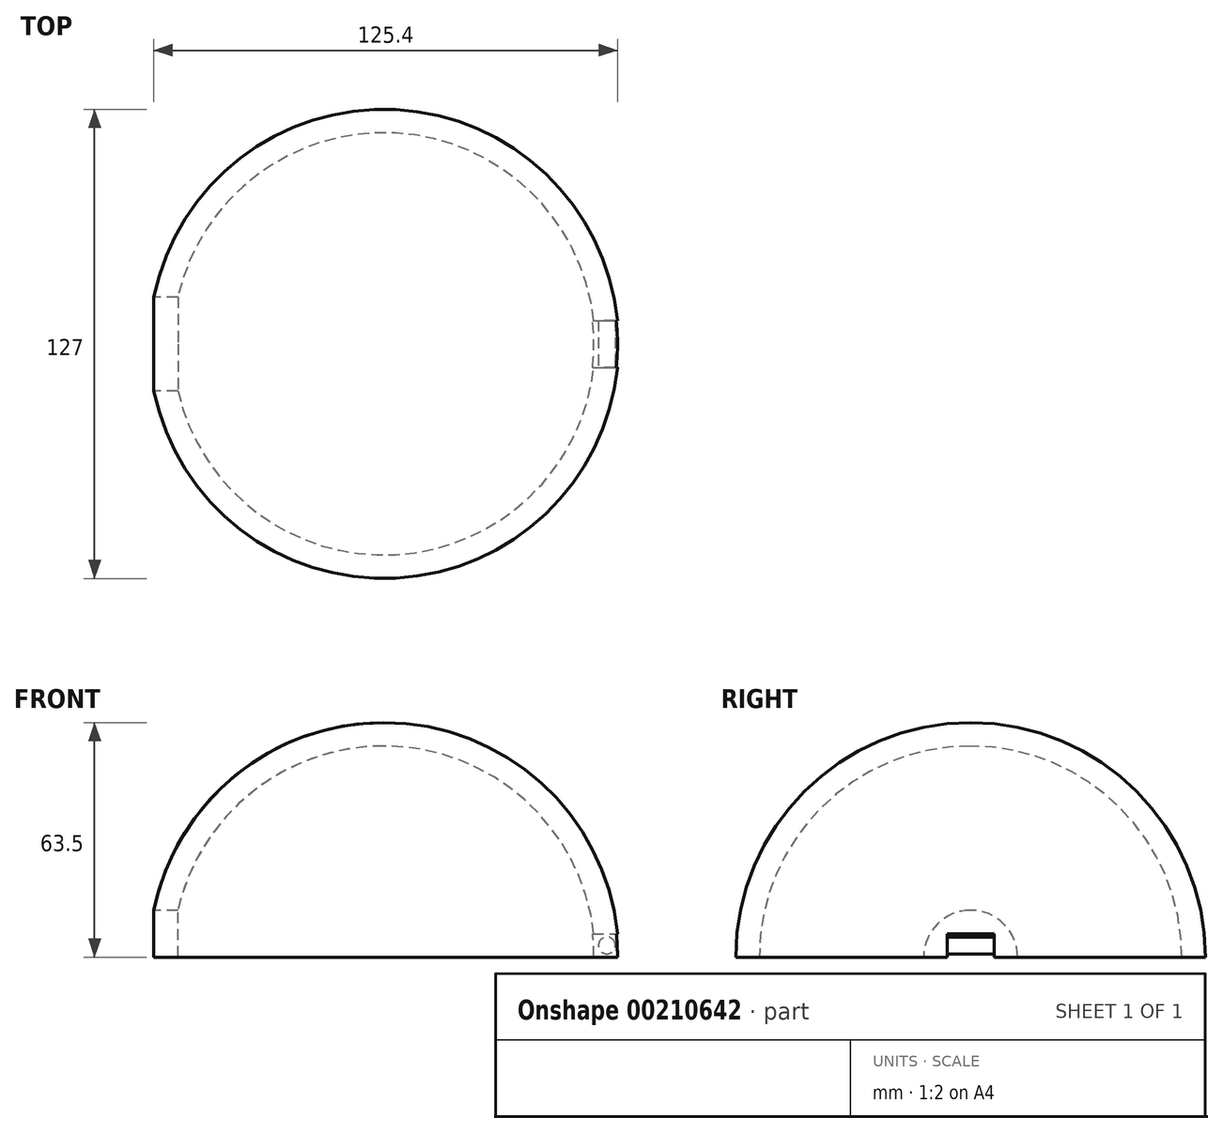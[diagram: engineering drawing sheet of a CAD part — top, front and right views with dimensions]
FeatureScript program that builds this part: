
annotation { "Feature Type Name" : "Feature", "Feature Type Description" : "" }
export const myFeature = defineFeature(function(context is Context, id is Id, definition is map)
    precondition{}
    {
        {
            var Q0;
            Q0=qCreatedBy(makeId("Front.planeOp"),FACE);
            var sketch = newSketch(context, id + "F0", { "sketchPlane" : qUnion([Q0])});
            skArc(sketch, "E0", {"start": v(0, 63.5) * mm, "mid": v(-44.9, 44.9) * mm, "end": v(-63.5, 0) * mm});
            skLineSegment(sketch, "E1", {"start": v(-63.5, 0) * mm, "end": v(-57.15, 0) * mm});
            skLineSegment(sketch, "E2", {"start": v(0, 57.15) * mm, "end": v(0, 63.5) * mm});
            skArc(sketch, "E3.0", {"start": v(0, 57.15) * mm, "mid": v(-40.41, 40.41) * mm, "end": v(-57.15, 0) * mm});
            skSolve(sketch);
        }
        {
            var Q0;
            Q0=makeQuery(id+"F0.imprint","IMPRINT",FACE,{"disambiguationData":[TD([[makeQuery(id+"F0.imprint","IMPRINT",EDGE,{"derivedFrom":sQuery(id+"F0.wireOp",EDGE,"E0")}),1.0]])]});
            var Q1;
            Q1=sQuery(id+"F0.wireOp",EDGE,"E2");
            revolve(context, id + "F1", {"entities" : qUnion([Q0]), "axis" : qUnion([Q1]), "revolveType" : RevolveType.FULL});
        }
        {
            var Q0;
            Q0=qCreatedBy(makeId("Front.planeOp"),FACE);
            var sketch = newSketch(context, id + "F2", { "sketchPlane" : qUnion([Q0])});
            skArc(sketch, "E4", {"start": v(63.5, 0) * mm, "mid": v(0, 63.5) * mm, "end": v(-63.5, 0) * mm, "construction": true});
            skArc(sketch, "E5", {"start": v(57.15, 0) * mm, "mid": v(0, 57.15) * mm, "end": v(-57.15, 0) * mm, "construction": true});
            skCircle(sketch, "E6", {"center": v(60.33, 3.17) * mm, "radius": 2.29 * mm});
            skLineSegment(sketch, "E7.bottom", {"start": v(55.18, -2) * mm, "end": v(65.36, -2) * mm});
            skLineSegment(sketch, "E7.top", {"start": v(55.18, 6.35) * mm, "end": v(65.36, 6.35) * mm});
            skLineSegment(sketch, "E7.left", {"start": v(55.18, -2) * mm, "end": v(55.18, 6.35) * mm});
            skLineSegment(sketch, "E7.right", {"start": v(65.36, -2) * mm, "end": v(65.36, 6.35) * mm});
            skSolve(sketch);
        }
        {
            var Q0;
            Q0=makeQuery(id+"F2.imprint","IMPRINT",FACE,{"disambiguationData":[TD([[makeQuery(id+"F2.imprint","IMPRINT",EDGE,{"derivedFrom":sQuery(id+"F2.wireOp",EDGE,"E6")}),-1.0]])]});
            extrude(context, id + "F3", {"entities" : qUnion([Q0]), "operationType" : NewBodyOperationType.REMOVE, "endBound" : BoundingType.SYMMETRIC, "oppositeDirection" : true, "depth" : 12.7 * mm});
        }
        {
            var Q0;
            Q0=qCreatedBy(makeId("Right.planeOp"),FACE);
            cPlane(context, id + "F4", {"entities" : qUnion([Q0]), "cplaneType" : CPlaneType.OFFSET, "offset" : 63.5 * mm, "oppositeDirection" : true, "width" : 152.4 * mm, "height" : 152.4 * mm});
        }
        {
            var Q0;
            Q0=qCreatedBy(id+"F4.planeOp",FACE);
            var sketch = newSketch(context, id + "F5", { "sketchPlane" : qUnion([Q0])});
            skCircle(sketch, "E8", {"center": v(0, 0) * mm, "radius": 12.7 * mm});
            skSolve(sketch);
        }
        {
            var Q0;
            Q0=makeQuery(id+"F5.imprint","IMPRINT",FACE,{"disambiguationData":[TD([[makeQuery(id+"F5.imprint","IMPRINT",EDGE,{"derivedFrom":sQuery(id+"F5.wireOp",EDGE,"E8")}),1.0]])]});
            extrude(context, id + "F6", {"entities" : qUnion([Q0]), "operationType" : NewBodyOperationType.REMOVE, "depth" : 25.4 * mm});
        }
    });
